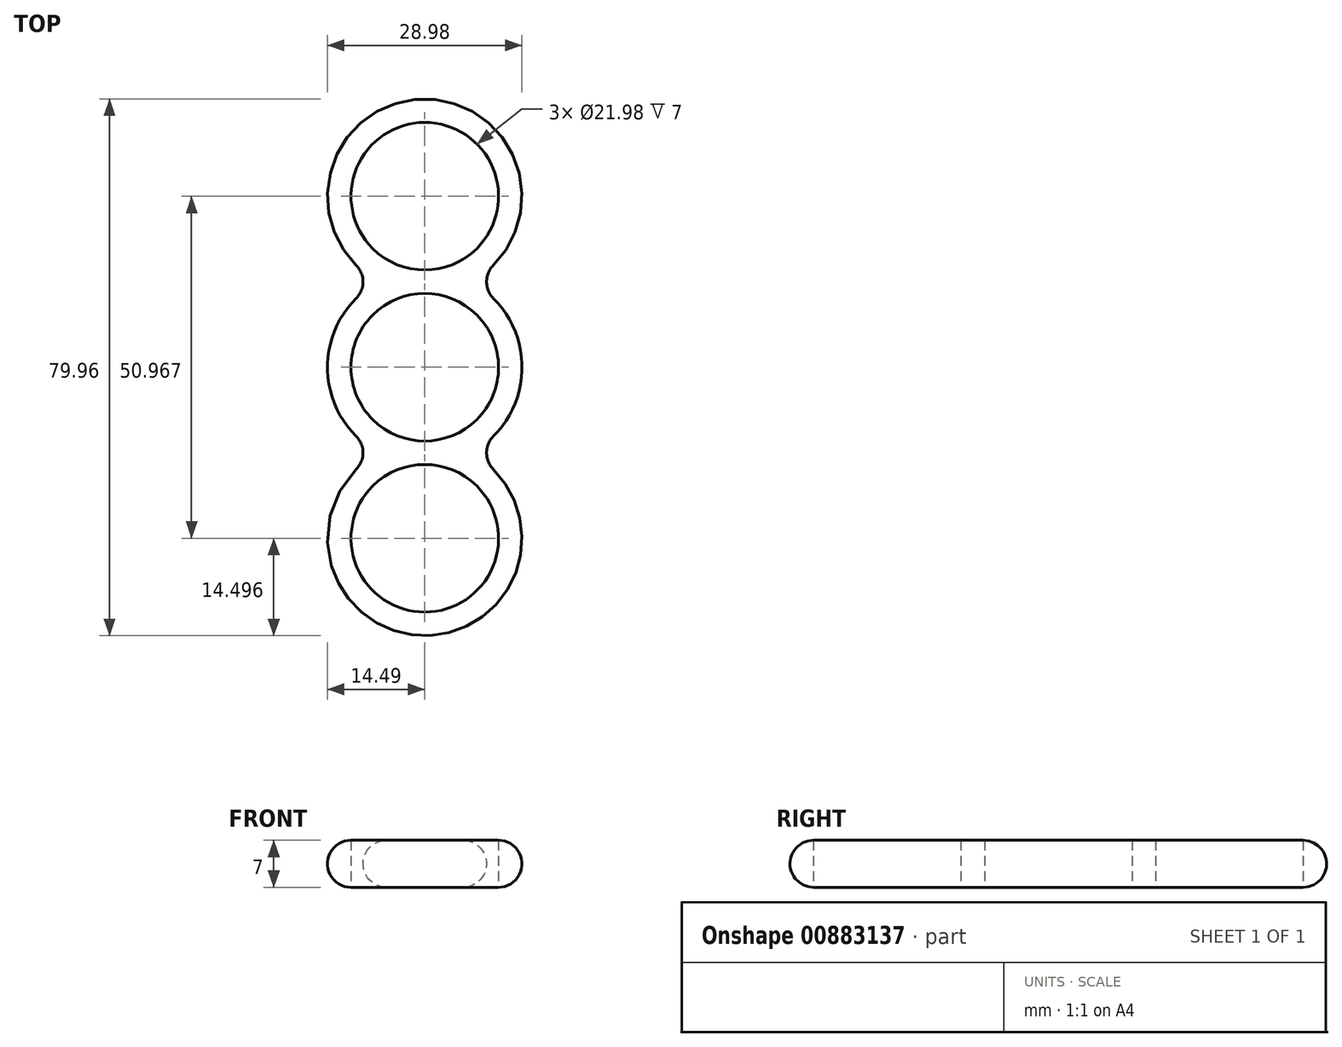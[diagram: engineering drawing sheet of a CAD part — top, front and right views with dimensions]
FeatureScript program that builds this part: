
annotation { "Feature Type Name" : "Feature", "Feature Type Description" : "" }
export const myFeature = defineFeature(function(context is Context, id is Id, definition is map)
    precondition{}
    {
        {
            var Q0;
            Q0=qCreatedBy(makeId("Top.planeOp"),FACE);
            var sketch = newSketch(context, id + "F0", { "sketchPlane" : qUnion([Q0])});
            skCircle(sketch, "E0", {"center": v(0, 0) * mm, "radius": 11 * mm});
            skCircle(sketch, "E1", {"center": v(0, 25.48) * mm, "radius": 11 * mm});
            skCircle(sketch, "E2", {"center": v(0, -25.48) * mm, "radius": 11 * mm});
            skLineSegment(sketch, "E3", {"start": v(0, 25.48) * mm, "end": v(0, -25.48) * mm, "construction": true});
            skLineSegment(sketch, "E4.bottom", {"start": v(-29.85, 57.15) * mm, "end": v(29.85, 57.15) * mm, "construction": true});
            skLineSegment(sketch, "E4.top", {"start": v(-29.85, -57.15) * mm, "end": v(29.85, -57.15) * mm, "construction": true});
            skLineSegment(sketch, "E4.left", {"start": v(-29.84, 57.15) * mm, "end": v(-29.85, -57.15) * mm, "construction": true});
            skLineSegment(sketch, "E4.right", {"start": v(29.85, 57.15) * mm, "end": v(29.84, -57.15) * mm, "construction": true});
            skPoint(sketch, "E5", {"position": v(0, 57.15) * mm});
            skPoint(sketch, "E6", {"position": v(-29.85, 0) * mm});
            skSolve(sketch);
        }
        {
            var Q0;
            Q0=qCreatedBy(makeId("Top.planeOp"),FACE);
            var sketch = newSketch(context, id + "F1", { "sketchPlane" : qUnion([Q0])});
            skCircle(sketch, "E7", {"center": v(0, 25.48) * mm, "radius": 11 * mm});
            skCircle(sketch, "E8", {"center": v(0, 0) * mm, "radius": 11 * mm});
            skCircle(sketch, "E9", {"center": v(0, -25.48) * mm, "radius": 11 * mm});
            skLineSegment(sketch, "E10.bottom", {"start": v(-29.85, 57.15) * mm, "end": v(29.84, 57.15) * mm, "construction": true});
            skLineSegment(sketch, "E10.top", {"start": v(-29.85, -57.15) * mm, "end": v(29.84, -57.15) * mm, "construction": true});
            skLineSegment(sketch, "E10.left", {"start": v(-29.85, 57.15) * mm, "end": v(-29.85, -57.15) * mm, "construction": true});
            skLineSegment(sketch, "E10.right", {"start": v(29.85, 57.15) * mm, "end": v(29.85, -57.15) * mm, "construction": true});
            skPoint(sketch, "E11", {"position": v(-29.85, 0) * mm});
            skPoint(sketch, "E12", {"position": v(0, 57.15) * mm});
            skArc(sketch, "E13.0", {"start": v(10.23, 15.22) * mm, "mid": v(0, 39.98) * mm, "end": v(-10.23, 15.22) * mm});
            skArc(sketch, "E14.0", {"start": v(-10.23, 10.26) * mm, "mid": v(-14.5, 0) * mm, "end": v(-10.23, -10.26) * mm});
            skArc(sketch, "E15.0", {"start": v(-10.23, -15.22) * mm, "mid": v(0, -39.98) * mm, "end": v(10.23, -15.22) * mm});
            skArc(sketch, "E16.trimOffspring", {"start": v(10.23, -10.26) * mm, "mid": v(14.5, 0) * mm, "end": v(10.23, 10.26) * mm});
            skPoint(sketch, "E17.visualSharp", {"position": v(-6.9, 12.74) * mm});
            skArc(sketch, "E17.filletArc", {"start": v(-10.23, 10.26) * mm, "mid": v(-9.2, 12.74) * mm, "end": v(-10.23, 15.22) * mm});
            skPoint(sketch, "E18.visualSharp", {"position": v(6.9, 12.74) * mm});
            skArc(sketch, "E18.filletArc", {"start": v(10.23, 15.22) * mm, "mid": v(9.2, 12.74) * mm, "end": v(10.23, 10.26) * mm});
            skPoint(sketch, "E19.visualSharp", {"position": v(6.9, -12.74) * mm});
            skArc(sketch, "E19.filletArc", {"start": v(10.23, -10.26) * mm, "mid": v(9.2, -12.74) * mm, "end": v(10.23, -15.22) * mm});
            skPoint(sketch, "E20.visualSharp", {"position": v(-6.9, -12.74) * mm});
            skArc(sketch, "E20.filletArc", {"start": v(-10.23, -15.22) * mm, "mid": v(-9.2, -12.74) * mm, "end": v(-10.23, -10.26) * mm});
            skPoint(sketch, "E21.end.orphan", {"position": v(10.23, 35.75) * mm});
            skSolve(sketch);
        }
        {
            var Q0;
            Q0=makeQuery(id+"F1.imprint","IMPRINT",FACE,{"disambiguationData":[TD([[makeQuery(id+"F1.imprint","IMPRINT",EDGE,{"derivedFrom":sQuery(id+"F1.wireOp",EDGE,"E7")}),-1.0]])]});
            extrude(context, id + "F2", {"entities" : qUnion([Q0]), "depth" : 7 * mm, "offsetDistance" : 25.4 * mm});
        }
        {
            var Q0;
            Q0=makeQuery(id+"F2.opExtrude","CAP_EDGE",EDGE,{"disambiguationData":[OSD([sQuery(id+"F1.wireOp",EDGE,"E16.trimOffspring")])],"isStart":false});
            var Q1;
            Q1=makeQuery(id+"F2.opExtrude","CAP_EDGE",EDGE,{"disambiguationData":[OSD([sQuery(id+"F1.wireOp",EDGE,"E19.filletArc")])],"isStart":true});
            var Q2;
            Q2=makeQuery(id+"F2.opExtrude","CAP_EDGE",EDGE,{"disambiguationData":[OSD([sQuery(id+"F1.wireOp",EDGE,"E15.0")])],"isStart":false});
            var Q3;
            Q3=makeQuery(id+"F2.opExtrude","CAP_EDGE",EDGE,{"disambiguationData":[OSD([sQuery(id+"F1.wireOp",EDGE,"E15.0")])],"isStart":true});
            fillet(context, id + "F3", {"entities" : qUnion([Q0, Q1, Q2, Q3]), "radius" : 3.5 * mm, "tangentPropagation" : true, "allowEdgeOverflow" : false});
        }
    });
